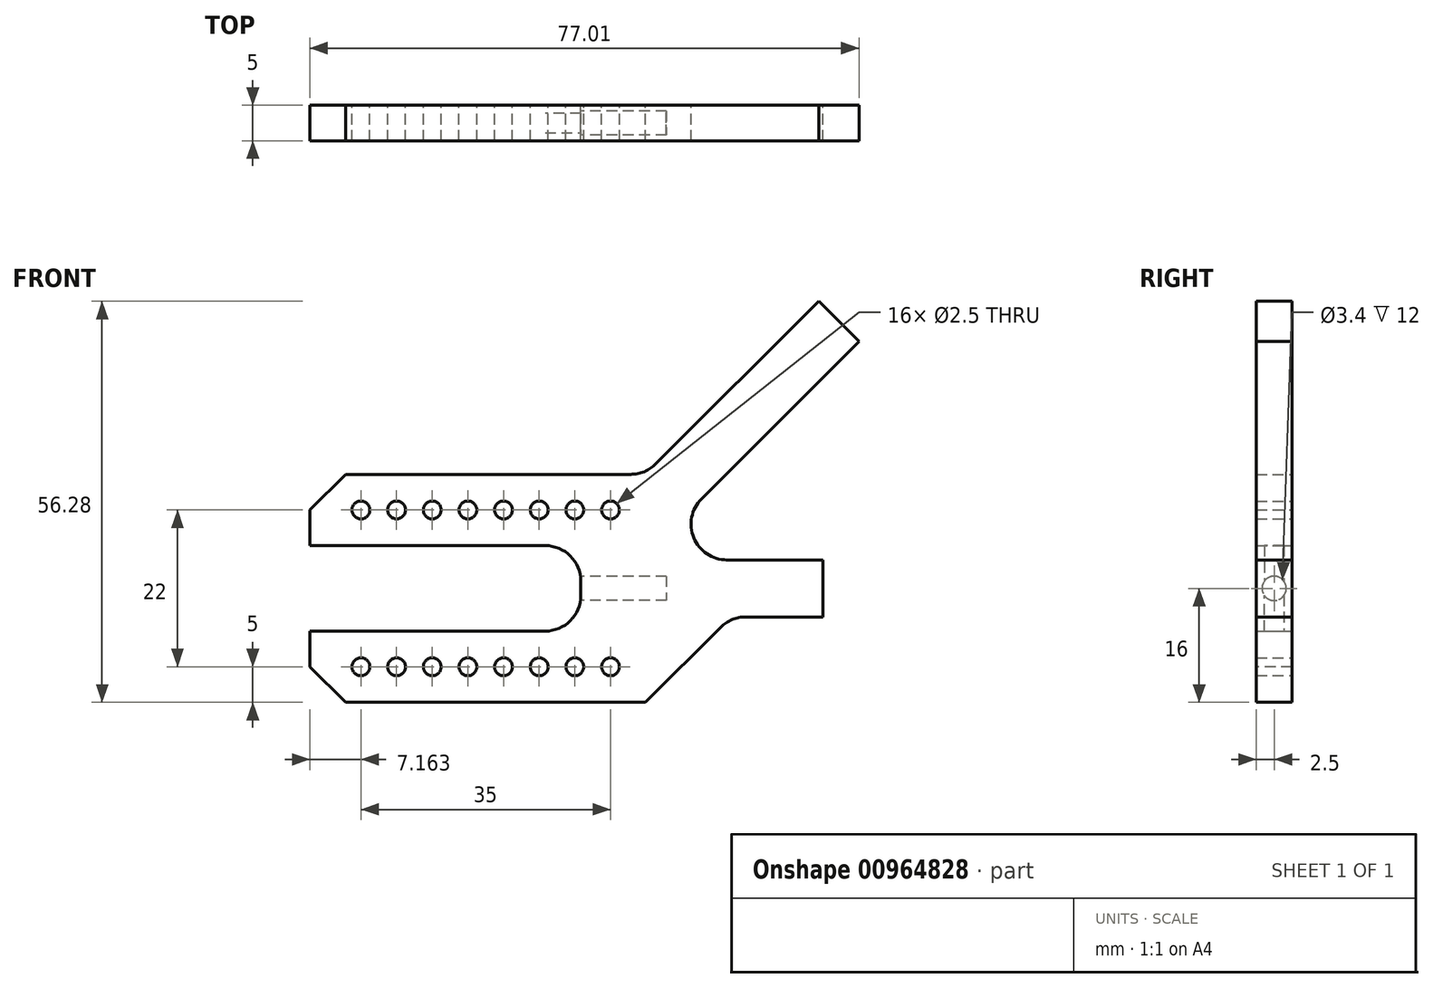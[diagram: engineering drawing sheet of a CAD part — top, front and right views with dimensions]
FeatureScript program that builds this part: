
annotation { "Feature Type Name" : "Feature", "Feature Type Description" : "" }
export const myFeature = defineFeature(function(context is Context, id is Id, definition is map)
    precondition{}
    {
        {
            var Q0;
            Q0=qCreatedBy(makeId("Front.planeOp"),FACE);
            var sketch = newSketch(context, id + "F0", { "sketchPlane" : qUnion([Q0])});
            skLineSegment(sketch, "E0.bottom", {"start": v(0, 0) * mm, "end": v(-50, 0) * mm});
            skLineSegment(sketch, "E0.top", {"start": v(0, 32) * mm, "end": v(-50, 32) * mm});
            skLineSegment(sketch, "E0.left", {"start": v(0, 0) * mm, "end": v(0, 32) * mm});
            skLineSegment(sketch, "E0.right", {"start": v(-50, 0) * mm, "end": v(-50, 10) * mm});
            skLineSegment(sketch, "E1.bottom", {"start": v(-12, 22) * mm, "end": v(-50, 22) * mm});
            skLineSegment(sketch, "E1.top", {"start": v(-12, 10) * mm, "end": v(-50, 10) * mm});
            skLineSegment(sketch, "E1.left", {"start": v(-12, 22) * mm, "end": v(-12, 10) * mm});
            skLineSegment(sketch, "E2.trimOffspring", {"start": v(-50, 22) * mm, "end": v(-50, 32) * mm});
            skLineSegment(sketch, "E3", {"start": v(37.42, 27) * mm, "end": v(-82.46, 27) * mm, "construction": true});
            skCircle(sketch, "E4", {"center": v(-42.84, 27) * mm, "radius": 1.25 * mm});
            skCircle(sketch, "E5.1.0.0", {"center": v(-37.84, 27) * mm, "radius": 1.25 * mm});
            skCircle(sketch, "E5.2.0.0", {"center": v(-32.84, 27) * mm, "radius": 1.25 * mm});
            skCircle(sketch, "E5.3.0.0", {"center": v(-27.84, 27) * mm, "radius": 1.25 * mm});
            skCircle(sketch, "E5.4.0.0", {"center": v(-22.84, 27) * mm, "radius": 1.25 * mm});
            skCircle(sketch, "E5.5.0.0", {"center": v(-17.84, 27) * mm, "radius": 1.25 * mm});
            skCircle(sketch, "E5.6.0.0", {"center": v(-12.84, 27) * mm, "radius": 1.25 * mm});
            skCircle(sketch, "E5.7.0.0", {"center": v(-7.84, 27) * mm, "radius": 1.25 * mm});
            skLineSegment(sketch, "E5.direction1", {"start": v(-42.84, 27) * mm, "end": v(-37.84, 27) * mm, "construction": true});
            skLineSegment(sketch, "E6", {"start": v(42.75, 16) * mm, "end": v(-102.21, 16) * mm, "construction": true});
            skCircle(sketch, "E7.MirrorC", {"center": v(-7.84, 5) * mm, "radius": 1.25 * mm});
            skCircle(sketch, "E8.MirrorC", {"center": v(-12.84, 5) * mm, "radius": 1.25 * mm});
            skCircle(sketch, "E9.MirrorC", {"center": v(-17.84, 5) * mm, "radius": 1.25 * mm});
            skCircle(sketch, "E10.MirrorC", {"center": v(-22.84, 5) * mm, "radius": 1.25 * mm});
            skCircle(sketch, "E11.MirrorC", {"center": v(-27.84, 5) * mm, "radius": 1.25 * mm});
            skCircle(sketch, "E12.MirrorC", {"center": v(-32.84, 5) * mm, "radius": 1.25 * mm});
            skCircle(sketch, "E13.MirrorC", {"center": v(-37.84, 5) * mm, "radius": 1.25 * mm});
            skCircle(sketch, "E14.MirrorC", {"center": v(-42.84, 5) * mm, "radius": 1.25 * mm});
            skSolve(sketch);
        }
        {
            var Q0;
            Q0 = qSketchRegion(id + "F0", true);
            extrude(context, id + "F1", {"entities" : qUnion([Q0]), "depth" : 5 * mm, "offsetDistance" : 25 * mm});
        }
        {
            var Q0;
            Q0=makeQuery(id+"F1.opExtrude","SWEPT_FACE",FACE,{"disambiguationData":[OSD([sQuery(id+"F0.wireOp",EDGE,"E1.left")])]});
            var sketch = newSketch(context, id + "F2", { "sketchPlane" : qUnion([Q0])});
            skPoint(sketch, "E15", {"position": v(2.5, 16) * mm});
            skPoint(sketch, "E15.positionSnap0", {"position": v(2.5, 22) * mm});
            skSolve(sketch);
        }
        {
            var Q0;
            Q0=sQuery(id+"F2.wireOp",VERTEX,"E15");
            var Q1;
            Q1=makeQuery(id+"F1.opExtrude","SWEPT_BODY",BODY,{"disambiguationData":[OSD([sQuery(id+"F0.wireOp",EDGE,"E0.bottom"),sQuery(id+"F0.wireOp",EDGE,"E0.top"),sQuery(id+"F0.wireOp",EDGE,"E0.left"),sQuery(id+"F0.wireOp",EDGE,"E0.right"),sQuery(id+"F0.wireOp",EDGE,"E1.bottom"),sQuery(id+"F0.wireOp",EDGE,"E1.top"),sQuery(id+"F0.wireOp",EDGE,"E1.left"),sQuery(id+"F0.wireOp",EDGE,"E2.trimOffspring"),sQuery(id+"F0.wireOp",EDGE,"E4"),sQuery(id+"F0.wireOp",EDGE,"E5.1.0.0"),sQuery(id+"F0.wireOp",EDGE,"E5.2.0.0"),sQuery(id+"F0.wireOp",EDGE,"E5.3.0.0"),sQuery(id+"F0.wireOp",EDGE,"E5.4.0.0"),sQuery(id+"F0.wireOp",EDGE,"E5.5.0.0"),sQuery(id+"F0.wireOp",EDGE,"E5.6.0.0"),sQuery(id+"F0.wireOp",EDGE,"E5.7.0.0"),sQuery(id+"F0.wireOp",EDGE,"E7.MirrorC"),sQuery(id+"F0.wireOp",EDGE,"E8.MirrorC"),sQuery(id+"F0.wireOp",EDGE,"E9.MirrorC"),sQuery(id+"F0.wireOp",EDGE,"E10.MirrorC"),sQuery(id+"F0.wireOp",EDGE,"E11.MirrorC"),sQuery(id+"F0.wireOp",EDGE,"E12.MirrorC"),sQuery(id+"F0.wireOp",EDGE,"E13.MirrorC"),sQuery(id+"F0.wireOp",EDGE,"E14.MirrorC")])]});
            hole(context, id + "F3", {"style" : HoleStyle.SIMPLE, "endStyle" : HoleEndStyle.THROUGH, "standardTappedOrClearance" : lookupTablePath({ "fit" : "Normal", "standard" : "ISO", "size" : "M3", "type" : "Clearance" }), "standardBlindInLast" : lookupTablePath({ "fit" : "Normal", "standard" : "ISO", "engagement" : "75%", "pitch" : "0.5 mm", "size" : "M3", "type" : "Clearance & tapped" }), "holeDiameter" : 3.4 * mm, "majorDiameter" : 5 * mm, "isTappedThrough" : true, "tappedDepth" : 12 * mm, "tapClearance" : 3, "locations" : qUnion([Q0]), "scope" : qUnion([Q1])});
        }
        {
            var Q0;
            Q0=makeQuery(id+"F1.opExtrude","SWEPT_EDGE",EDGE,{"disambiguationData":[OSD([sQuery(id+"F0.wireOp",EDGE,"E0.top"),sQuery(id+"F0.wireOp",EDGE,"E2.trimOffspring")])]});
            var Q1;
            Q1=makeQuery(id+"F1.opExtrude","SWEPT_EDGE",EDGE,{"disambiguationData":[OSD([sQuery(id+"F0.wireOp",EDGE,"E0.bottom"),sQuery(id+"F0.wireOp",EDGE,"E0.right")])]});
            chamfer(context, id + "F4", {"entities" : qUnion([Q0, Q1]), "width" : 5 * mm, "tangentPropagation" : true});
        }
        {
            var Q0;
            Q0=makeQuery(id+"F1.opExtrude","SWEPT_EDGE",EDGE,{"disambiguationData":[OSD([sQuery(id+"F0.wireOp",EDGE,"E1.bottom"),sQuery(id+"F0.wireOp",EDGE,"E1.left")])]});
            var Q1;
            Q1=makeQuery(id+"F1.opExtrude","SWEPT_EDGE",EDGE,{"disambiguationData":[OSD([sQuery(id+"F0.wireOp",EDGE,"E1.top"),sQuery(id+"F0.wireOp",EDGE,"E1.left")])]});
            fillet(context, id + "F5", {"entities" : qUnion([Q0, Q1]), "radius" : 5 * mm, "tangentPropagation" : true, "allowEdgeOverflow" : false});
        }
        {
            var Q0;
            Q0=qCreatedBy(makeId("Front.planeOp"),FACE);
            var sketch = newSketch(context, id + "F6", { "sketchPlane" : qUnion([Q0])});
            skLineSegment(sketch, "E16.top", {"start": v(0, 68.28) * mm, "end": v(37.82, 68.28) * mm});
            skLineSegment(sketch, "E16.left", {"start": v(0, 0) * mm, "end": v(0, 68.28) * mm});
            skLineSegment(sketch, "E16.right", {"start": v(37.82, 0) * mm, "end": v(37.82, 68.28) * mm});
            skLineSegment(sketch, "E17.top", {"start": v(37.82, -65.83) * mm, "end": v(0, -65.83) * mm});
            skLineSegment(sketch, "E17.left", {"start": v(37.82, 0) * mm, "end": v(37.82, -65.83) * mm});
            skLineSegment(sketch, "E17.right", {"start": v(0, 0) * mm, "end": v(0, -65.83) * mm});
            skSolve(sketch);
        }
        {
            var Q0;
            Q0=makeQuery(id+"F6.imprint","IMPRINT",FACE,{"disambiguationData":[TD([[makeQuery(id+"F6.imprint","IMPRINT",EDGE,{"derivedFrom":sQuery(id+"F6.wireOp",EDGE,"E16.top")}),-1.0]])]});
            extrude(context, id + "F7", {"entities" : qUnion([Q0]), "operationType" : NewBodyOperationType.ADD, "depth" : 5 * mm, "offsetDistance" : 25 * mm});
        }
        {
            var Q0;
            Q0=makeQuery(id+"F7.boolean.opBoolean","MERGE",FACE,{"derivedFrom":[makeQuery(id+"F1.opExtrude","CAP_FACE",FACE,{"disambiguationData":[OSD([sQuery(id+"F0.wireOp",EDGE,"E0.bottom"),sQuery(id+"F0.wireOp",EDGE,"E0.top"),sQuery(id+"F0.wireOp",EDGE,"E0.left"),sQuery(id+"F0.wireOp",EDGE,"E0.right"),sQuery(id+"F0.wireOp",EDGE,"E1.bottom"),sQuery(id+"F0.wireOp",EDGE,"E1.top"),sQuery(id+"F0.wireOp",EDGE,"E1.left"),sQuery(id+"F0.wireOp",EDGE,"E2.trimOffspring"),sQuery(id+"F0.wireOp",EDGE,"E4"),sQuery(id+"F0.wireOp",EDGE,"E5.1.0.0"),sQuery(id+"F0.wireOp",EDGE,"E5.2.0.0"),sQuery(id+"F0.wireOp",EDGE,"E5.3.0.0"),sQuery(id+"F0.wireOp",EDGE,"E5.4.0.0"),sQuery(id+"F0.wireOp",EDGE,"E5.5.0.0"),sQuery(id+"F0.wireOp",EDGE,"E5.6.0.0"),sQuery(id+"F0.wireOp",EDGE,"E5.7.0.0"),sQuery(id+"F0.wireOp",EDGE,"E7.MirrorC"),sQuery(id+"F0.wireOp",EDGE,"E8.MirrorC"),sQuery(id+"F0.wireOp",EDGE,"E9.MirrorC"),sQuery(id+"F0.wireOp",EDGE,"E10.MirrorC"),sQuery(id+"F0.wireOp",EDGE,"E11.MirrorC"),sQuery(id+"F0.wireOp",EDGE,"E12.MirrorC"),sQuery(id+"F0.wireOp",EDGE,"E13.MirrorC"),sQuery(id+"F0.wireOp",EDGE,"E14.MirrorC")])],"isStart":true}),makeQuery(id+"F7.opExtrude","CAP_FACE",FACE,{"disambiguationData":[OSD([sQuery(id+"F6.wireOp",EDGE,"E16.top"),sQuery(id+"F6.wireOp",EDGE,"E16.left"),sQuery(id+"F6.wireOp",EDGE,"E16.right"),sQuery(id+"F6.wireOp",EDGE,"E17.top"),sQuery(id+"F6.wireOp",EDGE,"E17.left"),sQuery(id+"F6.wireOp",EDGE,"E17.right")])],"isStart":true})]});
            var sketch = newSketch(context, id + "F8", { "sketchPlane" : qUnion([Q0])});
            skLineSegment(sketch, "E18", {"start": v(-21.93, 20) * mm, "end": v(-8.45, 20) * mm});
            skLineSegment(sketch, "E19", {"start": v(-21.93, 12) * mm, "end": v(-11.14, 12) * mm});
            skLineSegment(sketch, "E20", {"start": v(-21.93, 20) * mm, "end": v(-21.93, 12) * mm});
            skPoint(sketch, "E21.start.orphan", {"position": v(-21.93, 32) * mm});
            skPoint(sketch, "E22.orphan", {"position": v(0, 12) * mm});
            skLineSegment(sketch, "E23", {"start": v(0, 20) * mm, "end": v(0, 23.62) * mm});
            skLineSegment(sketch, "E24", {"start": v(-4.92, 28.54) * mm, "end": v(-27, 50.62) * mm});
            skLineSegment(sketch, "E25", {"start": v(-27, 50.62) * mm, "end": v(-21.35, 56.28) * mm});
            skLineSegment(sketch, "E26", {"start": v(-21.35, 56.28) * mm, "end": v(1.47, 33.46) * mm});
            skLineSegment(sketch, "E27", {"start": v(2.93, 32) * mm, "end": v(18.11, 32) * mm});
            skLineSegment(sketch, "E28", {"start": v(5, 32) * mm, "end": v(18.11, 32) * mm});
            skLineSegment(sketch, "E29", {"start": v(2.93, 32) * mm, "end": v(2.93, -8.51) * mm, "construction": true});
            skLineSegment(sketch, "E30", {"start": v(2.93, 0) * mm, "end": v(-7.6, 10.54) * mm});
            skPoint(sketch, "E31.visualSharp", {"position": v(3.62, 20) * mm});
            skArc(sketch, "E31.filletArc", {"start": v(-8.45, 20) * mm, "mid": v(-3.83, 23.09) * mm, "end": v(-4.92, 28.54) * mm});
            skPoint(sketch, "E32.visualSharp", {"position": v(-9.07, 12) * mm});
            skArc(sketch, "E32.filletArc", {"start": v(-7.6, 10.54) * mm, "mid": v(-9.23, 11.62) * mm, "end": v(-11.14, 12) * mm});
            skPoint(sketch, "E33.visualSharp", {"position": v(2.93, 32) * mm});
            skArc(sketch, "E33.filletArc", {"start": v(1.47, 33.46) * mm, "mid": v(3.09, 32.38) * mm, "end": v(5, 32) * mm});
            skSolve(sketch);
        }
        {
            var Q0;
            Q0=makeQuery(id+"F8.imprint","IMPRINT",FACE,{"disambiguationData":[TD([[makeQuery(id+"F8.imprint","IMPRINT",EDGE,{"derivedFrom":sQuery(id+"F8.wireOp",EDGE,"E18")}),1.0]])]});
            extrude(context, id + "F9", {"entities" : qUnion([Q0]), "operationType" : NewBodyOperationType.REMOVE, "oppositeDirection" : true, "depth" : 25 * mm, "offsetDistance" : 25 * mm});
        }
        {
            var Q0;
            Q0=makeQuery(id+"F7.boolean.opBoolean","MERGE",FACE,{"derivedFrom":[makeQuery(id+"F1.opExtrude","CAP_FACE",FACE,{"disambiguationData":[OSD([sQuery(id+"F0.wireOp",EDGE,"E0.bottom"),sQuery(id+"F0.wireOp",EDGE,"E0.top"),sQuery(id+"F0.wireOp",EDGE,"E0.left"),sQuery(id+"F0.wireOp",EDGE,"E0.right"),sQuery(id+"F0.wireOp",EDGE,"E1.bottom"),sQuery(id+"F0.wireOp",EDGE,"E1.top"),sQuery(id+"F0.wireOp",EDGE,"E1.left"),sQuery(id+"F0.wireOp",EDGE,"E2.trimOffspring"),sQuery(id+"F0.wireOp",EDGE,"E4"),sQuery(id+"F0.wireOp",EDGE,"E5.1.0.0"),sQuery(id+"F0.wireOp",EDGE,"E5.2.0.0"),sQuery(id+"F0.wireOp",EDGE,"E5.3.0.0"),sQuery(id+"F0.wireOp",EDGE,"E5.4.0.0"),sQuery(id+"F0.wireOp",EDGE,"E5.5.0.0"),sQuery(id+"F0.wireOp",EDGE,"E5.6.0.0"),sQuery(id+"F0.wireOp",EDGE,"E5.7.0.0"),sQuery(id+"F0.wireOp",EDGE,"E7.MirrorC"),sQuery(id+"F0.wireOp",EDGE,"E8.MirrorC"),sQuery(id+"F0.wireOp",EDGE,"E9.MirrorC"),sQuery(id+"F0.wireOp",EDGE,"E10.MirrorC"),sQuery(id+"F0.wireOp",EDGE,"E11.MirrorC"),sQuery(id+"F0.wireOp",EDGE,"E12.MirrorC"),sQuery(id+"F0.wireOp",EDGE,"E13.MirrorC"),sQuery(id+"F0.wireOp",EDGE,"E14.MirrorC")])],"isStart":true}),makeQuery(id+"F7.opExtrude","CAP_FACE",FACE,{"disambiguationData":[OSD([sQuery(id+"F6.wireOp",EDGE,"E16.top"),sQuery(id+"F6.wireOp",EDGE,"E16.left"),sQuery(id+"F6.wireOp",EDGE,"E16.right"),sQuery(id+"F6.wireOp",EDGE,"E17.top"),sQuery(id+"F6.wireOp",EDGE,"E17.left"),sQuery(id+"F6.wireOp",EDGE,"E17.right")])],"isStart":true})]});
            var sketch = newSketch(context, id + "F10", { "sketchPlane" : qUnion([Q0])});
            skLineSegment(sketch, "E34", {"start": v(0, 34.93) * mm, "end": v(1.47, 33.46) * mm});
            skArc(sketch, "E35.filletArc", {"start": v(1.47, 33.46) * mm, "mid": v(3.09, 32.38) * mm, "end": v(5, 32) * mm});
            skLineSegment(sketch, "E36", {"start": v(0, 34.93) * mm, "end": v(0, 32) * mm});
            skLineSegment(sketch, "E37", {"start": v(0, 32) * mm, "end": v(5, 32) * mm});
            skSolve(sketch);
        }
        {
            var Q0;
            Q0 = qSketchRegion(id + "F10", true);
            extrude(context, id + "F11", {"entities" : qUnion([Q0]), "operationType" : NewBodyOperationType.ADD, "oppositeDirection" : true, "depth" : 5 * mm, "offsetDistance" : 25 * mm});
        }
    });
